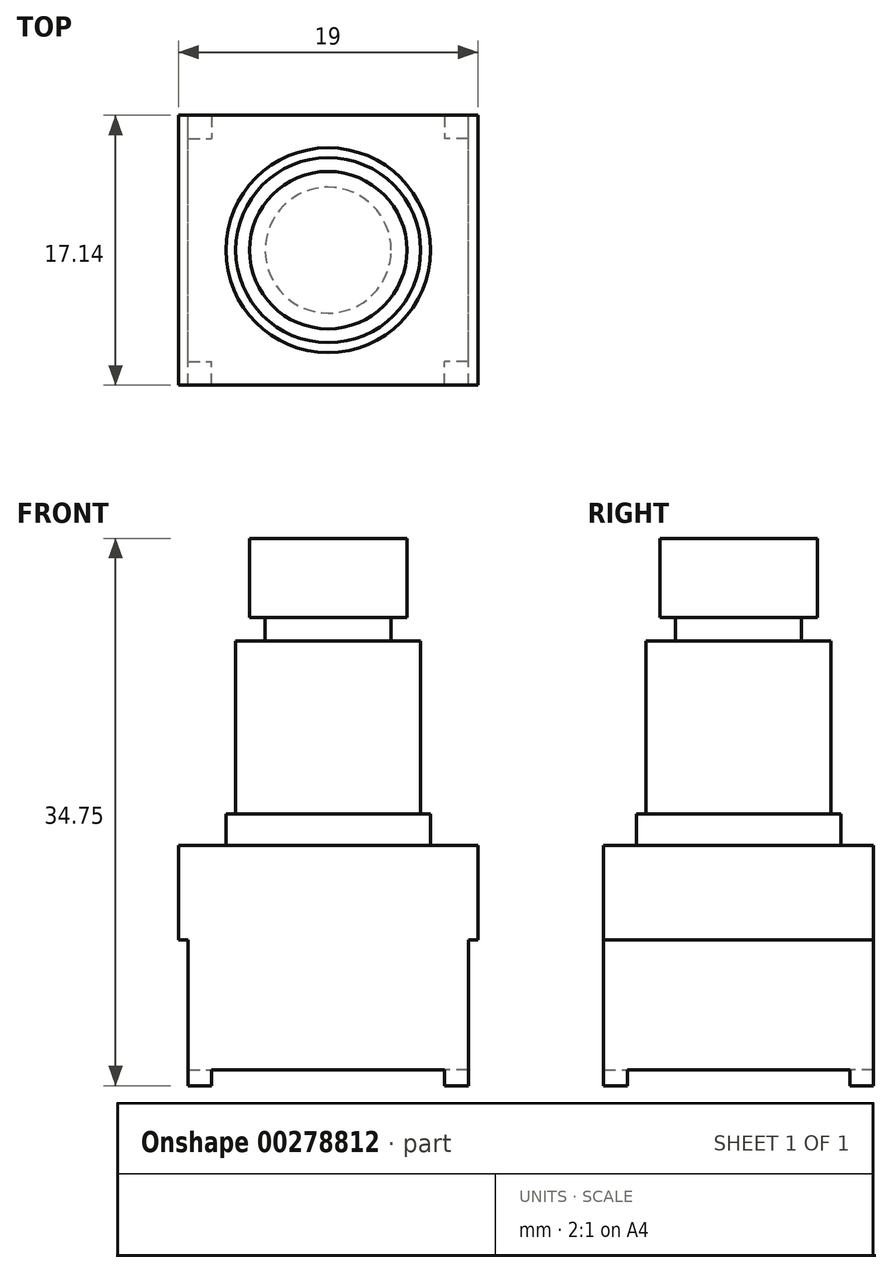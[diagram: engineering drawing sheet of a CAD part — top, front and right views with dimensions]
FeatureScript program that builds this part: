
annotation { "Feature Type Name" : "Feature", "Feature Type Description" : "" }
export const myFeature = defineFeature(function(context is Context, id is Id, definition is map)
    precondition{}
    {
        {
            var Q0;
            Q0=qCreatedBy(makeId("Top.planeOp"),FACE);
            var sketch = newSketch(context, id + "F0", { "sketchPlane" : qUnion([Q0])});
            skLineSegment(sketch, "E0.bottom", {"start": v(9.5, 8.58) * mm, "end": v(-9.5, 8.58) * mm});
            skLineSegment(sketch, "E0.top", {"start": v(9.5, -8.57) * mm, "end": v(-9.5, -8.57) * mm});
            skLineSegment(sketch, "E0.left", {"start": v(9.5, 8.58) * mm, "end": v(9.5, -8.57) * mm});
            skLineSegment(sketch, "E0.right", {"start": v(-9.5, 8.58) * mm, "end": v(-9.5, -8.57) * mm});
            skPoint(sketch, "E0.middle", {"position": v(0, 0) * mm});
            skSolve(sketch);
        }
        {
            var Q0;
            Q0=qSketchRegion(id+"F0",true);
            extrude(context, id + "F1", {"entities" : qUnion([Q0]), "depth" : 6 * mm});
        }
        {
            var Q0;
            Q0=makeQuery(id+"F1.opExtrude","CAP_FACE",FACE,{"disambiguationData":[OSD([sQuery(id+"F0.wireOp",EDGE,"E0.bottom"),sQuery(id+"F0.wireOp",EDGE,"E0.top"),sQuery(id+"F0.wireOp",EDGE,"E0.left"),sQuery(id+"F0.wireOp",EDGE,"E0.right")])],"isStart":true});
            var sketch = newSketch(context, id + "F2", { "sketchPlane" : qUnion([Q0])});
            skLineSegment(sketch, "E1.bottom", {"start": v(8.9, 8.57) * mm, "end": v(-8.9, 8.57) * mm});
            skLineSegment(sketch, "E1.top", {"start": v(8.9, -8.57) * mm, "end": v(-8.9, -8.57) * mm});
            skLineSegment(sketch, "E1.left", {"start": v(8.9, 8.57) * mm, "end": v(8.9, -8.57) * mm});
            skLineSegment(sketch, "E1.right", {"start": v(-8.9, 8.57) * mm, "end": v(-8.9, -8.57) * mm});
            skPoint(sketch, "E1.middle", {"position": v(0, 0) * mm});
            skSolve(sketch);
        }
        {
            var Q0;
            Q0=qSketchRegion(id+"F2",true);
            extrude(context, id + "F3", {"entities" : qUnion([Q0]), "operationType" : NewBodyOperationType.ADD, "depth" : 8.25 * mm});
        }
        {
            var Q0;
            Q0=makeQuery(id+"F3.opExtrude","CAP_FACE",FACE,{"disambiguationData":[OSD([sQuery(id+"F2.wireOp",EDGE,"E1.bottom"),sQuery(id+"F2.wireOp",EDGE,"E1.top"),sQuery(id+"F2.wireOp",EDGE,"E1.left"),sQuery(id+"F2.wireOp",EDGE,"E1.right")])],"isStart":false});
            var sketch = newSketch(context, id + "F4", { "sketchPlane" : qUnion([Q0])});
            skLineSegment(sketch, "E2.bottom", {"start": v(-8.9, 8.57) * mm, "end": v(-7.4, 8.57) * mm});
            skLineSegment(sketch, "E2.top", {"start": v(-8.9, 7.07) * mm, "end": v(-7.4, 7.07) * mm});
            skLineSegment(sketch, "E2.left", {"start": v(-8.9, 8.57) * mm, "end": v(-8.9, 7.07) * mm});
            skLineSegment(sketch, "E2.right", {"start": v(-7.4, 8.57) * mm, "end": v(-7.4, 7.07) * mm});
            skLineSegment(sketch, "E3.bottom", {"start": v(8.9, 8.57) * mm, "end": v(7.4, 8.57) * mm});
            skLineSegment(sketch, "E3.top", {"start": v(8.9, 7.07) * mm, "end": v(7.4, 7.07) * mm});
            skLineSegment(sketch, "E3.left", {"start": v(8.9, 8.57) * mm, "end": v(8.9, 7.07) * mm});
            skLineSegment(sketch, "E3.right", {"start": v(7.4, 8.57) * mm, "end": v(7.4, 7.07) * mm});
            skLineSegment(sketch, "E4.bottom", {"start": v(-8.9, -8.58) * mm, "end": v(-7.4, -8.58) * mm});
            skLineSegment(sketch, "E4.top", {"start": v(-8.9, -7.08) * mm, "end": v(-7.4, -7.08) * mm});
            skLineSegment(sketch, "E4.left", {"start": v(-8.9, -8.58) * mm, "end": v(-8.9, -7.08) * mm});
            skLineSegment(sketch, "E4.right", {"start": v(-7.4, -8.58) * mm, "end": v(-7.4, -7.08) * mm});
            skLineSegment(sketch, "E5.bottom", {"start": v(8.9, -8.58) * mm, "end": v(7.4, -8.58) * mm});
            skLineSegment(sketch, "E5.top", {"start": v(8.9, -7.08) * mm, "end": v(7.4, -7.08) * mm});
            skLineSegment(sketch, "E5.left", {"start": v(8.9, -8.58) * mm, "end": v(8.9, -7.08) * mm});
            skLineSegment(sketch, "E5.right", {"start": v(7.4, -8.58) * mm, "end": v(7.4, -7.08) * mm});
            skSolve(sketch);
        }
        {
            var Q0;
            Q0=qSketchRegion(id+"F4",true);
            extrude(context, id + "F5", {"entities" : qUnion([Q0]), "operationType" : NewBodyOperationType.ADD, "depth" : 1 * mm});
        }
        {
            var Q0;
            Q0=makeQuery(id+"F1.opExtrude","CAP_FACE",FACE,{"disambiguationData":[OSD([sQuery(id+"F0.wireOp",EDGE,"E0.bottom"),sQuery(id+"F0.wireOp",EDGE,"E0.top"),sQuery(id+"F0.wireOp",EDGE,"E0.left"),sQuery(id+"F0.wireOp",EDGE,"E0.right")])],"isStart":false});
            var sketch = newSketch(context, id + "F6", { "sketchPlane" : qUnion([Q0])});
            skCircle(sketch, "E6", {"center": v(0, 0) * mm, "radius": 6.5 * mm});
            skSolve(sketch);
        }
        {
            var Q0;
            Q0=qSketchRegion(id+"F6",true);
            extrude(context, id + "F7", {"entities" : qUnion([Q0]), "depth" : 2 * mm});
        }
        {
            var Q0;
            Q0=makeQuery(id+"F7.opExtrude","CAP_FACE",FACE,{"disambiguationData":[OSD([sQuery(id+"F6.wireOp",EDGE,"E6")])],"isStart":false});
            var sketch = newSketch(context, id + "F8", { "sketchPlane" : qUnion([Q0])});
            skCircle(sketch, "E7", {"center": v(0, 0) * mm, "radius": 5.88 * mm});
            skSolve(sketch);
        }
        {
            var Q0;
            Q0=qSketchRegion(id+"F8",true);
            extrude(context, id + "F9", {"entities" : qUnion([Q0]), "operationType" : NewBodyOperationType.ADD, "depth" : 11 * mm});
        }
        {
            var Q0;
            Q0=makeQuery(id+"F9.opExtrude","CAP_FACE",FACE,{"disambiguationData":[OSD([sQuery(id+"F8.wireOp",EDGE,"E7")])],"isStart":false});
            var sketch = newSketch(context, id + "F10", { "sketchPlane" : qUnion([Q0])});
            skCircle(sketch, "E8", {"center": v(0, 0) * mm, "radius": 4 * mm});
            skSolve(sketch);
        }
        {
            var Q0;
            Q0=qSketchRegion(id+"F10",true);
            extrude(context, id + "F11", {"entities" : qUnion([Q0]), "operationType" : NewBodyOperationType.ADD, "depth" : 1.5 * mm});
        }
        {
            var Q0;
            Q0=makeQuery(id+"F11.opExtrude","CAP_FACE",FACE,{"disambiguationData":[OSD([sQuery(id+"F10.wireOp",EDGE,"E8")])],"isStart":false});
            var sketch = newSketch(context, id + "F12", { "sketchPlane" : qUnion([Q0])});
            skCircle(sketch, "E9", {"center": v(0, 0) * mm, "radius": 5 * mm});
            skSolve(sketch);
        }
        {
            var Q0;
            Q0=qSketchRegion(id+"F12",true);
            extrude(context, id + "F13", {"entities" : qUnion([Q0]), "operationType" : NewBodyOperationType.ADD, "depth" : 5 * mm});
        }
    });
